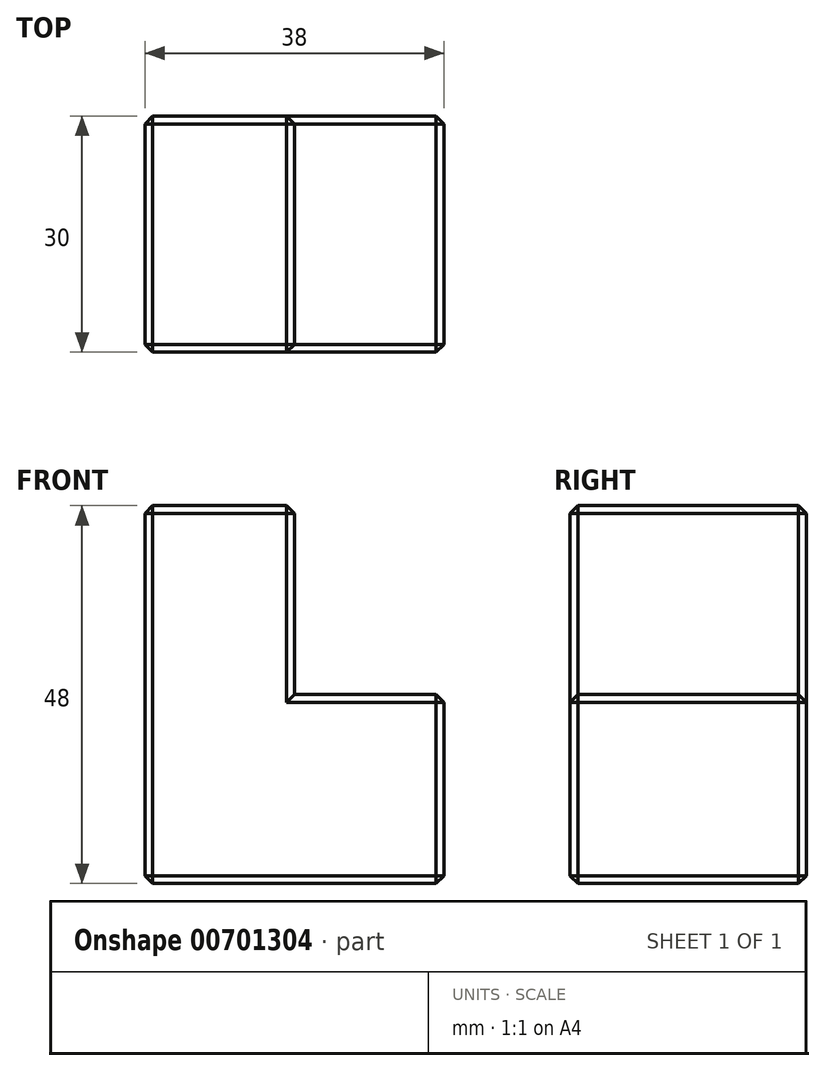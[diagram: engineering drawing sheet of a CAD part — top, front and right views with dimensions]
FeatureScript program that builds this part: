
annotation { "Feature Type Name" : "Feature", "Feature Type Description" : "" }
export const myFeature = defineFeature(function(context is Context, id is Id, definition is map)
    precondition{}
    {
        {
            var Q0;
            Q0=qCreatedBy(makeId("Front.planeOp"),FACE);
            var sketch = newSketch(context, id + "F0", { "sketchPlane" : qUnion([Q0])});
            skLineSegment(sketch, "E0", {"start": v(0, 0) * mm, "end": v(0, 24) * mm});
            skLineSegment(sketch, "E1", {"start": v(0, 24) * mm, "end": v(-19, 24) * mm});
            skLineSegment(sketch, "E2", {"start": v(-19, 24) * mm, "end": v(-19, -24) * mm});
            skLineSegment(sketch, "E3", {"start": v(-19, -24) * mm, "end": v(19, -24) * mm});
            skLineSegment(sketch, "E4", {"start": v(19, -24) * mm, "end": v(19, 0) * mm});
            skLineSegment(sketch, "E5", {"start": v(19, 0) * mm, "end": v(0, 0) * mm});
            skSolve(sketch);
        }
        {
            var Q0;
            Q0 = qSketchRegion(id + "F0", true);
            extrude(context, id + "F1", {"entities" : qUnion([Q0]), "depth" : 30 * mm, "offsetDistance" : 25 * mm});
        }
        {
            var Q0;
            Q0=makeQuery(id+"F1.opExtrude","CAP_FACE",FACE,{"disambiguationData":[OSD([sQuery(id+"F0.wireOp",EDGE,"D9Z5CcDY-DNmw-xolN-zCWf-u0buZa3Zb7D3.bottom"),sQuery(id+"F0.wireOp",EDGE,"D9Z5CcDY-DNmw-xolN-zCWf-u0buZa3Zb7D3.left"),sQuery(id+"F0.wireOp",EDGE,"NQsJeWaB-7gva-BVsU-hbTY-Mn5as9p5fRou.bottom"),sQuery(id+"F0.wireOp",EDGE,"NQsJeWaB-7gva-BVsU-hbTY-Mn5as9p5fRou.top"),sQuery(id+"F0.wireOp",EDGE,"NQsJeWaB-7gva-BVsU-hbTY-Mn5as9p5fRou.left"),sQuery(id+"F0.wireOp",EDGE,"NQsJeWaB-7gva-BVsU-hbTY-Mn5as9p5fRou.right")])],"isStart":false});
            var Q1;
            Q1=makeQuery(id+"F1.opExtrude","CAP_FACE",FACE,{"disambiguationData":[OSD([sQuery(id+"F0.wireOp",EDGE,"D9Z5CcDY-DNmw-xolN-zCWf-u0buZa3Zb7D3.bottom"),sQuery(id+"F0.wireOp",EDGE,"D9Z5CcDY-DNmw-xolN-zCWf-u0buZa3Zb7D3.left"),sQuery(id+"F0.wireOp",EDGE,"NQsJeWaB-7gva-BVsU-hbTY-Mn5as9p5fRou.bottom"),sQuery(id+"F0.wireOp",EDGE,"NQsJeWaB-7gva-BVsU-hbTY-Mn5as9p5fRou.top"),sQuery(id+"F0.wireOp",EDGE,"NQsJeWaB-7gva-BVsU-hbTY-Mn5as9p5fRou.left"),sQuery(id+"F0.wireOp",EDGE,"NQsJeWaB-7gva-BVsU-hbTY-Mn5as9p5fRou.right")])],"isStart":true});
            var Q2;
            Q2=makeQuery(id+"F1.opExtrude","SWEPT_FACE",FACE,{"disambiguationData":[OSD([sQuery(id+"F0.wireOp",EDGE,"NQsJeWaB-7gva-BVsU-hbTY-Mn5as9p5fRou.bottom")])]});
            var Q3;
            Q3=makeQuery(id+"F1.opExtrude","SWEPT_FACE",FACE,{"disambiguationData":[OSD([sQuery(id+"F0.wireOp",EDGE,"NQsJeWaB-7gva-BVsU-hbTY-Mn5as9p5fRou.top")])]});
            var Q4;
            Q4=makeQuery(id+"F1.opExtrude","SWEPT_EDGE",EDGE,{"disambiguationData":[OSD([sQuery(id+"F0.wireOp",EDGE,"D9Z5CcDY-DNmw-xolN-zCWf-u0buZa3Zb7D3.bottom"),sQuery(id+"F0.wireOp",EDGE,"NQsJeWaB-7gva-BVsU-hbTY-Mn5as9p5fRou.left")])]});
            var Q5;
            Q5=makeQuery(id+"F1.opExtrude","CAP_FACE",FACE,{"disambiguationData":[OSD([sQuery(id+"F0.wireOp",EDGE,"E0"),sQuery(id+"F0.wireOp",EDGE,"E1"),sQuery(id+"F0.wireOp",EDGE,"E2"),sQuery(id+"F0.wireOp",EDGE,"E3"),sQuery(id+"F0.wireOp",EDGE,"E4"),sQuery(id+"F0.wireOp",EDGE,"E5")])],"isStart":false});
            var Q6;
            Q6=makeQuery(id+"F1.opExtrude","CAP_FACE",FACE,{"disambiguationData":[OSD([sQuery(id+"F0.wireOp",EDGE,"E0"),sQuery(id+"F0.wireOp",EDGE,"E1"),sQuery(id+"F0.wireOp",EDGE,"E2"),sQuery(id+"F0.wireOp",EDGE,"E3"),sQuery(id+"F0.wireOp",EDGE,"E4"),sQuery(id+"F0.wireOp",EDGE,"E5")])],"isStart":true});
            var Q7;
            Q7=makeQuery(id+"F1.opExtrude","SWEPT_FACE",FACE,{"disambiguationData":[OSD([sQuery(id+"F0.wireOp",EDGE,"E1")])]});
            var Q8;
            Q8=makeQuery(id+"F1.opExtrude","SWEPT_FACE",FACE,{"disambiguationData":[OSD([sQuery(id+"F0.wireOp",EDGE,"E3")])]});
            var Q9;
            Q9=makeQuery(id+"F1.opExtrude","SWEPT_EDGE",EDGE,{"disambiguationData":[OSD([sQuery(id+"F0.wireOp",EDGE,"E4"),sQuery(id+"F0.wireOp",EDGE,"E5")])]});
            chamfer(context, id + "F2", {"entities" : qUnion([Q0, Q1, Q2, Q3, Q4, Q5, Q6, Q7, Q8, Q9]), "width" : 1 * mm, "tangentPropagation" : true});
        }
    });
